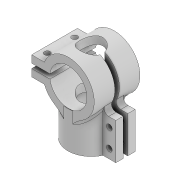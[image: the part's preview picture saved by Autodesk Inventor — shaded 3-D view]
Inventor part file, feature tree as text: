
AUTODESK INVENTOR PART (.ipt)
format: ipt  version: 2022 (Build 260153000, 153)  size: 337,408 bytes
history: native  units: mm
features: extrude x5, sketch x4, fillet x1
ambient origin geometry x8: Origin, YZ Plane, XZ Plane, XY Plane, X Axis, Y Axis, Z Axis, Center Point
bodies: Solid1 (feature_tree)
feature tree (10):
  sketch  "Sketch1"  dims[d0=35.0mm d1=8.0mm]
  extrude  "Extrusion1"  Depth=8.0mm
  extrude  "Extrusion4"  Depth=8.0mm
  extrude  "Extrusion5"  Depth=2.5mm
  fillet  "Fillet1"  Radius=20.0mm
  extrude  "Extrusion6"  Depth=10.0mm TaperAngle=0.0deg
  extrude  "Extrusion7"  Depth=10.0mm
  sketch  "Sketch4"  dims[d2=8.0mm d3=8.0mm]
  sketch  "Sketch5"  dims[d7=2.5mm d8=2.5mm d9=20.0mm]
  sketch  "Sketch6"  dims[d10=20.0mm d11=40.0mm d12=0.0mm d24=40.5mm d25=8.0mm d26=8.0mm d27=8.0mm d28=20.0mm d29=20.0mm d30=2.5mm d31=50.0mm d32=0.0mm d33=100.0mm d34=0.0mm d35=25.0mm d36=5.0mm d37=6.2mm d38=6.2mm d39=10.0mm d40=10.0mm d41=7.0mm d42=7.0mm d43=100.0mm d44=0.0mm d45=6.2mm d46=6.2mm d47=7.0mm d48=7.0mm d49=10.0mm d50=10.0mm d51=100.0mm d52=0.0mm]
